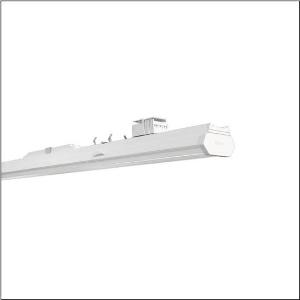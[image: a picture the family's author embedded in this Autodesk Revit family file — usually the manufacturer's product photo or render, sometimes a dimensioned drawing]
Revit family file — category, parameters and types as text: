
# Revit family: licross_r__21_protected_ho_52tp13mn4fxs_ad58
name_source: partatom
category: Lighting Fixtures
units: mm (PartAtom-declared; Revit-internal decimal feet)

## family parameters
Cut with Voids When Loaded = No
Host = Face
Light Source = No
Part Type = Normal
Room Calculation Point = No
Round Connector Dimension = Use Diameter
Shared = No

## types (1)
- --- (1 x LED, 15060 lm, 83.2 W, 4000K)
    Apparent Load = 83 VA
    CIE Flux Codes = 89 96 99 100 99
    Color Rendering = 80
    Color Temperature = 4000K
    Default Elevation = 1800 mm
    Description = Licross® 21 Protected HO, luminaire insert, of sheet steel, galvanised, coil coated, white, length: 1.500mm, width: 66mm, height: 67mm, LED rated luminous flux: 15.060lm, light colour: 840, control gear: ON/OFF Multilumen, with plug, 3-pole, with phase selection, mains connection: 220..240V, AC, 50/60Hz, rated input power: 83W, halogen-free wiring, primary light control with lens, of plastic, primary optical cover: cover, of PMMA, light emission: direct distribution, primary light characteristic: symmetric, protection rating (complete): IP64, insulation class (complete): insulation class I (protective earthing), certification: CE, ENEC, VDE, UKCA, protection symbol: D if used in an environment with conductive dust loads with corresponding accessories, impact resistance: IK06, permissible ambient temperature for indoor applications: -35..+35°C, corresponds to IFS (International Featured Standards) requirements for safety and quality in the food industry, reducing of maximum allowable ambient temperature of 5°C with ceiling mounting, LABS conformity tested according to VDMA 24364:2018-05, packaging unit: 1 piece
    Height = 92 mm
    Lamp = 1 x LED
    Lamp Light Flux = 15060 lm
    Lamp Power = 83.2 W
    Lamp count = 1
    Length = 1500 mm
    Luminous efficacy = 181 lm/W
    Manufacturer = Siteco
    ModVariant = No
    Model = 52TP13MN4FXS
    Mounting Place = Ceiling
    Mounting Type = Pendant
    Number of Poles = 1
    OnlyDefault = Yes
    Power Factor = 1
    Product Name = Licross® 21 Protected HO
    Product group = luminaire insert
    ProductGroupID = 901
    Protection Class = Protection class I
    Protection Degree = IP 64
    RLX_Detail_Level = 1
    RLX_Emergency_Light_Flux = 0 lm
    RLX_Emergency_Type = 0
    RLX_Emergency_Type_DB = No
    RlxData = <blob elided: 21909 chars, md5=70002ba1>
    Socket = socket
    Standby Power = 0 W
    System Light Flux = 15060 lm
    System Power = 83 W
    Type Comments = factory setting: luminous flux: 100 % | (A | C | E) | 195 mA
    Type Image = l_1256148.jpg
    URL = http://relux.com
    VarID = @adj_077877
    Voltage = 0 V
    Weight = 0.00 kg
    Width = 88 mm

## geometry (parser evidence)
native form markers: Blend x4, Sweep x9
no freeform markers — native parametric forms only
